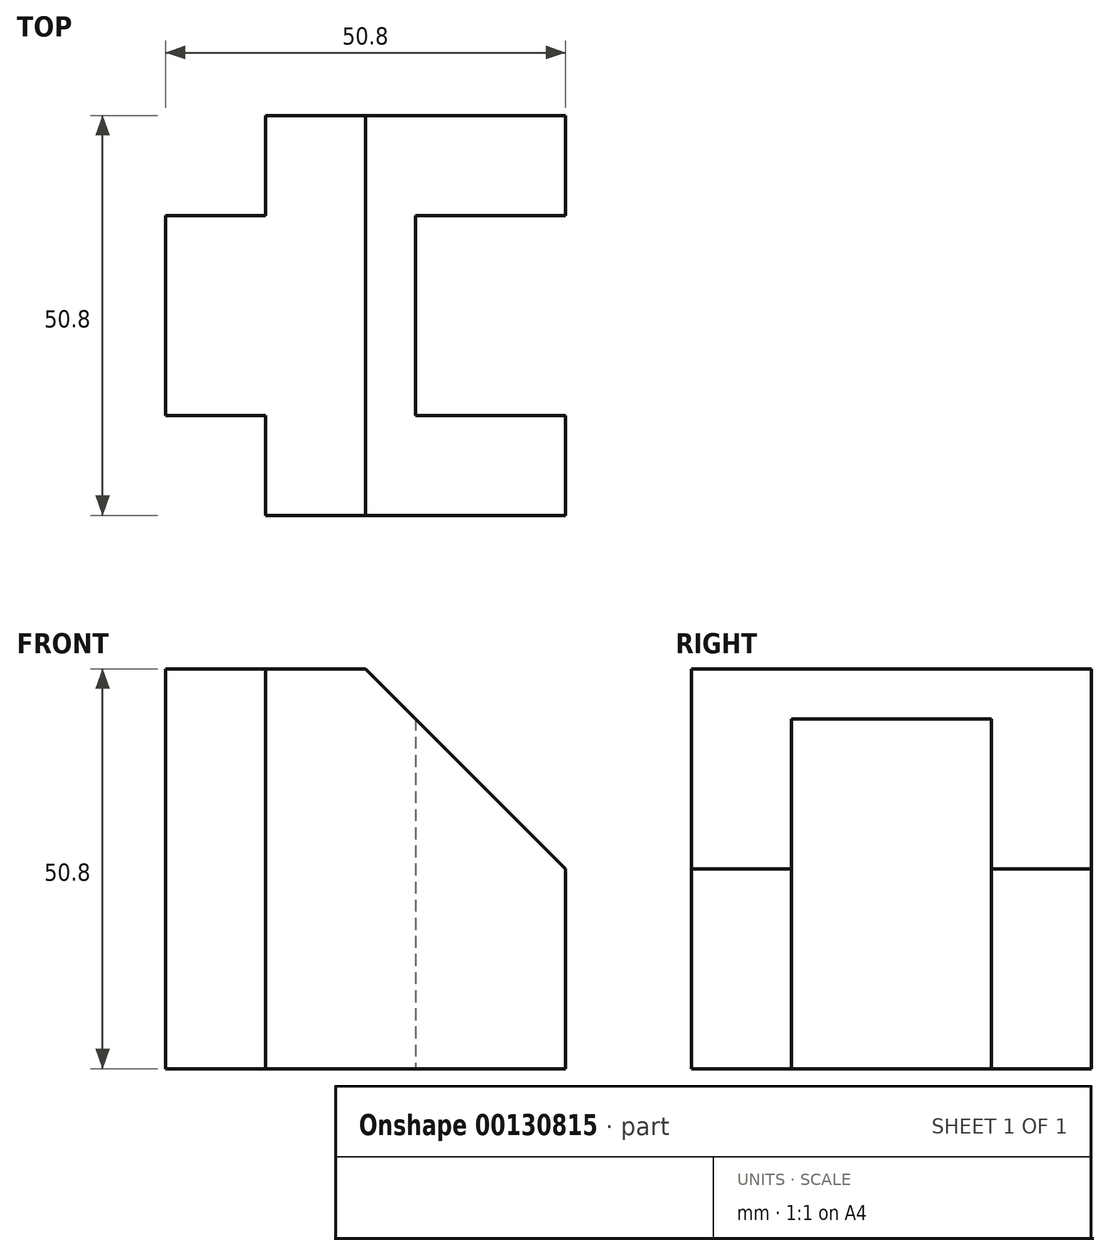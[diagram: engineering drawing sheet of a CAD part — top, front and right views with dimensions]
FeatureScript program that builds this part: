
annotation { "Feature Type Name" : "Feature", "Feature Type Description" : "" }
export const myFeature = defineFeature(function(context is Context, id is Id, definition is map)
    precondition{}
    {
        {
            var Q0;
            Q0=qCreatedBy(makeId("Top.planeOp"),FACE);
            var sketch = newSketch(context, id + "F0", { "sketchPlane" : qUnion([Q0])});
            skLineSegment(sketch, "E0", {"start": v(0, 0) * mm, "end": v(38.1, 0) * mm});
            skLineSegment(sketch, "E1", {"start": v(38.1, 0) * mm, "end": v(38.1, 12.7) * mm});
            skLineSegment(sketch, "E2", {"start": v(38.1, 12.7) * mm, "end": v(19.05, 12.7) * mm});
            skLineSegment(sketch, "E3", {"start": v(19.05, 12.7) * mm, "end": v(19.05, 38.1) * mm});
            skLineSegment(sketch, "E4", {"start": v(19.05, 38.1) * mm, "end": v(38.1, 38.1) * mm});
            skLineSegment(sketch, "E5", {"start": v(38.1, 38.1) * mm, "end": v(38.1, 50.8) * mm});
            skLineSegment(sketch, "E6", {"start": v(38.1, 50.8) * mm, "end": v(0, 50.8) * mm});
            skLineSegment(sketch, "E7", {"start": v(0, 50.8) * mm, "end": v(0, 38.1) * mm});
            skLineSegment(sketch, "E8", {"start": v(0, 38.1) * mm, "end": v(-12.7, 38.1) * mm});
            skLineSegment(sketch, "E9", {"start": v(-12.7, 38.1) * mm, "end": v(-12.7, 12.7) * mm});
            skLineSegment(sketch, "E10", {"start": v(-12.7, 12.7) * mm, "end": v(0, 12.7) * mm});
            skLineSegment(sketch, "E11", {"start": v(0, 12.7) * mm, "end": v(0, 0) * mm});
            skLineSegment(sketch, "E12", {"start": v(12.7, 0) * mm, "end": v(12.7, 50.8) * mm});
            skSolve(sketch);
        }
        {
            var Q0;
            {var subQ0=sQuery(id+"F0.wireOp",EDGE,"E7");Q0=makeQuery(id+"F0.imprint","IMPRINT",FACE,{"disambiguationData":[TD([[makeQuery(id+"F0.imprint","IMPRINT",EDGE,{"derivedFrom":subQ0}),1.0]])]});}
            var Q1;
            {var subQ0=sQuery(id+"F0.wireOp",EDGE,"E1");Q1=makeQuery(id+"F0.imprint","IMPRINT",FACE,{"disambiguationData":[TD([[makeQuery(id+"F0.imprint","IMPRINT",EDGE,{"derivedFrom":subQ0}),1.0]])]});}
            extrude(context, id + "F1", {"entities" : qUnion([Q0, Q1]), "depth" : 50.8 * mm});
        }
        {
            var Q0;
            Q0=makeQuery(id+"F1.opExtrude","SWEPT_FACE",FACE,{"disambiguationData":[OSD([sQuery(id+"F0.wireOp",EDGE,"E0")])]});
            var sketch = newSketch(context, id + "F2", { "sketchPlane" : qUnion([Q0])});
            skLineSegment(sketch, "E13.0", {"start": v(0, 50.8) * mm, "end": v(38.1, 50.8) * mm});
            skLineSegment(sketch, "E14.0.0", {"start": v(0, 0) * mm, "end": v(38.1, 0) * mm});
            skLineSegment(sketch, "E14.0.1", {"start": v(38.1, 0) * mm, "end": v(38.1, 50.8) * mm});
            skLineSegment(sketch, "E14.0.2", {"start": v(38.1, 50.8) * mm, "end": v(0, 50.8) * mm});
            skLineSegment(sketch, "E14.0.3", {"start": v(0, 50.8) * mm, "end": v(0, 0) * mm});
            skLineSegment(sketch, "E15", {"start": v(12.7, 50.8) * mm, "end": v(38.1, 25.4) * mm});
            skSolve(sketch);
        }
        {
            var Q0;
            {var subQ3=sQuery(id+"F2.wireOp",EDGE,"E15");Q0=makeQuery(id+"F2.imprint","IMPRINT",FACE,{"disambiguationData":[TD([[makeQuery(id+"F2.imprint","IMPRINT",EDGE,{"derivedFrom":subQ3}),1.0]])]});}
            extrude(context, id + "F3", {"entities" : qUnion([Q0]), "operationType" : NewBodyOperationType.REMOVE, "endBound" : BoundingType.THROUGH_ALL, "oppositeDirection" : true, "depth" : 25.4 * mm});
        }
    });
